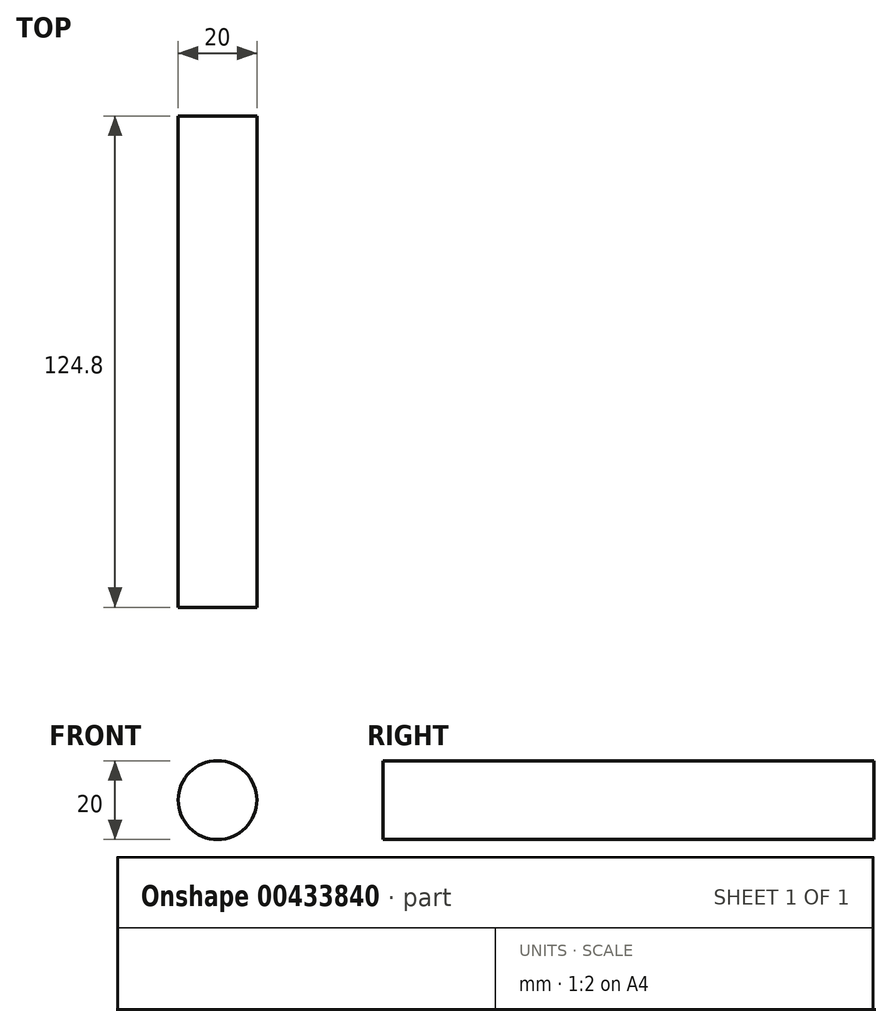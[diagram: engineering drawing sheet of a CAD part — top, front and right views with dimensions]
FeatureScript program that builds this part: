
annotation { "Feature Type Name" : "Feature", "Feature Type Description" : "" }
export const myFeature = defineFeature(function(context is Context, id is Id, definition is map)
    precondition{}
    {
        {
            var Q0;
            Q0=qCreatedBy(makeId("Front.planeOp"),FACE);
            var sketch = newSketch(context, id + "F0", { "sketchPlane" : qUnion([Q0])});
            skCircle(sketch, "E0", {"center": v(0, 0) * mm, "radius": 10 * mm});
            skSolve(sketch);
        }
        {
            var Q0;
            Q0 = qSketchRegion(id + "F0", true);
            extrude(context, id + "F1", {"entities" : qUnion([Q0]), "oppositeDirection" : true, "depth" : 124.8 * mm, "offsetDistance" : 25 * mm});
        }
    });
